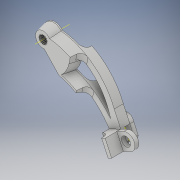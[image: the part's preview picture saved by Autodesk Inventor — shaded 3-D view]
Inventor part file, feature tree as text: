
AUTODESK INVENTOR PART (.ipt)
format: ipt  version: 2018 (Build 220112000, 112)  size: 461,312 bytes
history: native  units: in
note: dims shown in document units (in); Inventor stores cm internally (conversion verified against a paired STEP export)
features: sketch x15, extrude x12, fillet x2, plane x1, other x1, pattern_circular x1
ambient origin geometry x8: Origin, YZ Plane, XZ Plane, XY Plane, X Axis, Y Axis, Z Axis, Center Point
bodies: Solid1 (feature_tree)
feature tree (32):
  sketch  "Sketch1"  dims[d15=1.0in d47=0.1969in d48=0.1969in]
  extrude  "Extrusion12"  Depth=0.1969in
  sketch  "Sketch16"  dims[d63=2.1654in d64=0.1969in]
  extrude  "Extrusion16"  Depth=0.1969in
  extrude  "Extrusion19"  Depth=0.1969in
  plane  "Work Plane9"
  sketch  "Sketch25"  dims[d75=0.2559in d76=0.2756in d77=0.0in]
  sketch  "Sketch26"  dims[d101=0.1181in d102=0.3937in d103=0.0in d106=0.5906in]
  extrude  "Extrusion20"  Depth=0.1969in
  sketch  "Sketch30"  dims[d118=0.4724in d119=0.1181in]
  extrude  "Extrusion21"  Depth=0.2756in TaperAngle=0.0deg
  extrude  "Extrusion22"  Depth=0.3937in TaperAngle=0.0deg
  fillet  "Fillet5"  Radius=0.5906in
  extrude  "Extrusion25"  Depth=0.1575in TaperAngle=0.0deg
  extrude  "Extrusion26"  Depth=0.1181in
  extrude  "Extrusion27"  Depth=0.2165in
  extrude  "Extrusion29"  Depth=0.315in TaperAngle=0.0deg
  extrude  "Extrusion30"  Depth=0.1181in
  fillet  "Fillet12"  Radius=0.2362in
  extrude  "Extrusion31"  Depth=0.4724in TaperAngle=0.0deg
  other  "Work Axis1"
  pattern_circular  "Circular Pattern1"  [2 undecoded]
  sketch  "Sketch19"  dims[d65=0.1969in d66=0.7874in]
  sketch  "Sketch24"  dims[d68=0.1969in d74=0.1969in]
  sketch  "Sketch27"  dims[d115=0.5906in d116=0.1575in d117=0.0in]
  sketch  "Sketch31"  dims[d120=0.374in d121=0.2165in]
  sketch  "Sketch32"  dims[d122=0.2362in d123=0.315in d124=0.0in]
  sketch  "Sketch35"  dims[d129=0.2362in d130=0.1181in d131=0.2362in]
  sketch  "Sketch37"  dims[d132=0.1181in d133=0.4724in d134=0.0in]
  sketch  "Sketch39"  dims[d135=0.1516in d136=0.0in]
  sketch  "Sketch40"  dims[d139=0.1969in]
  sketch  "Sketch41"  dims[d140=0.2756in d141=0.1181in d142=0.0in d143=0.2362in d153=0.2756in d154=0.0in d155=0.1181in d156=0.0in d157=1.7717in d158=0.2362in d159=0.0in d166=1.7717in d167=0.315in d168=-0.0825in d173=0.315in d174=0.0in d175=0.1181in d176=0.1575in d177=0.2559in d178=0.1378in d179=0.1969in d181=0.0236in d182=0.0098in d183=0.0197in d184=0.0295in d185=0.0079in d186=0.0354in d187=0.0197in d188=0.0197in d189=0.3543in d190=0.0in d191=7.0866in d192=360.0deg]
note: 2 required parameter values undecoded (feature->parameter linkage not recoverable at this tier; creation-order binding heuristic only, values carry confidence <= 0.55)
